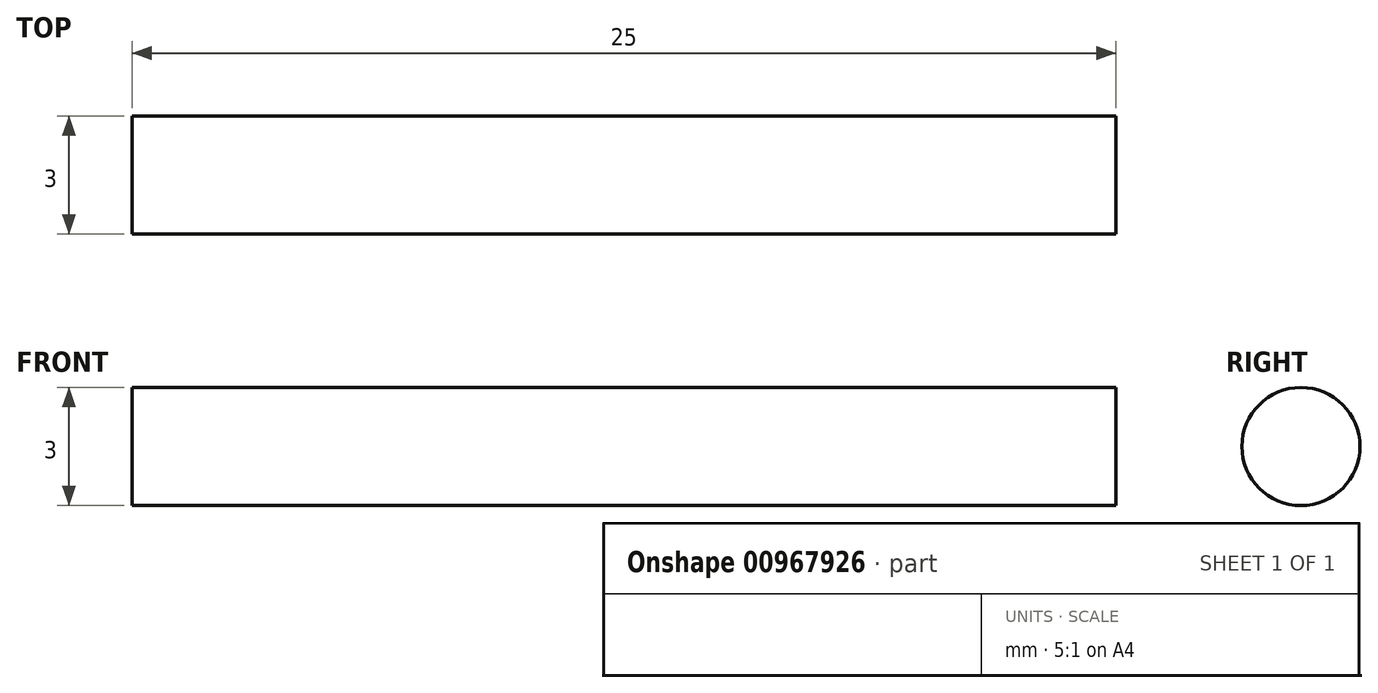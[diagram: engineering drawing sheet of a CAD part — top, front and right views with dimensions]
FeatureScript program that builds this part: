
annotation { "Feature Type Name" : "Feature", "Feature Type Description" : "" }
export const myFeature = defineFeature(function(context is Context, id is Id, definition is map)
    precondition{}
    {
        {
            var Q0;
            Q0=qCreatedBy(makeId("Right.planeOp"),FACE);
            var sketch = newSketch(context, id + "F0", { "sketchPlane" : qUnion([Q0])});
            skCircle(sketch, "E0", {"center": v(0, 0) * mm, "radius": 1.5 * mm});
            skSolve(sketch);
        }
        {
            var Q0;
            Q0 = qSketchRegion(id + "F0", true);
            extrude(context, id + "F1", {"entities" : qUnion([Q0]), "depth" : 25 * mm, "offsetDistance" : 25 * mm});
        }
    });
